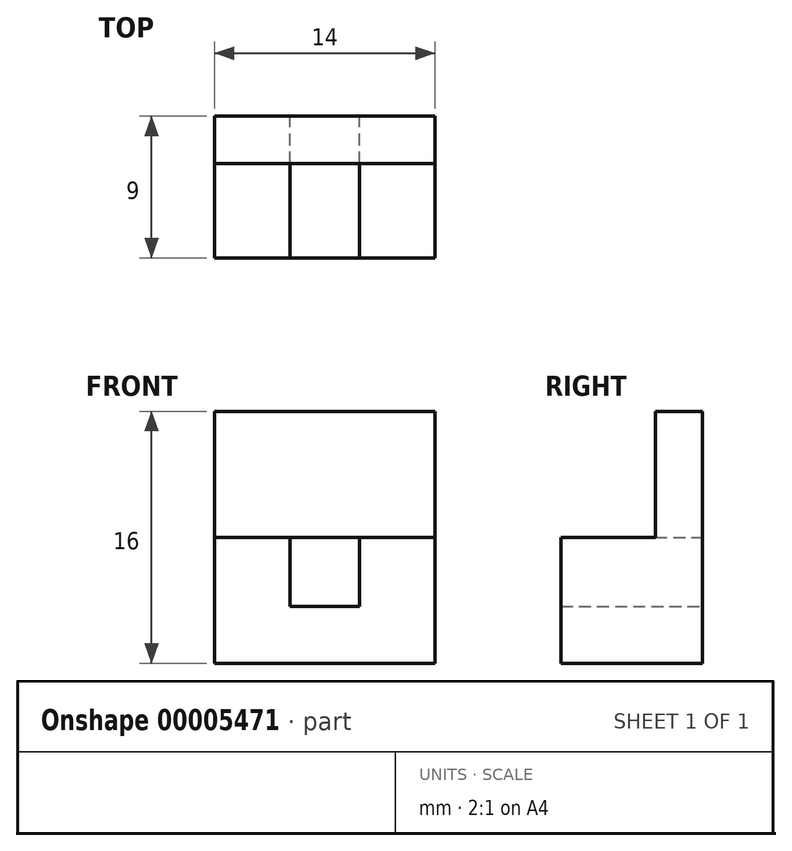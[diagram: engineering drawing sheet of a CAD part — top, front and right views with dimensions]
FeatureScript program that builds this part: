
annotation { "Feature Type Name" : "Feature", "Feature Type Description" : "" }
export const myFeature = defineFeature(function(context is Context, id is Id, definition is map)
    precondition{}
    {
        {
            var Q0;
            Q0=qCreatedBy(makeId("Front.planeOp"),FACE);
            var sketch = newSketch(context, id + "F0", { "sketchPlane" : qUnion([Q0])});
            skCircle(sketch, "E0.cCircle", {"center": v(0, 0) * mm, "radius": 2.2 * mm, "construction": true});
            skLineSegment(sketch, "E0.0", {"start": v(-2.2, 2.2) * mm, "end": v(2.2, 2.2) * mm});
            skLineSegment(sketch, "E0.1", {"start": v(2.2, 2.2) * mm, "end": v(2.2, -2.2) * mm});
            skLineSegment(sketch, "E0.2", {"start": v(2.2, -2.2) * mm, "end": v(-2.2, -2.2) * mm});
            skLineSegment(sketch, "E0.3", {"start": v(-2.2, -2.2) * mm, "end": v(-2.2, 2.2) * mm});
            skPoint(sketch, "E0.0.midPoint", {"position": v(0, 2.2) * mm});
            skLineSegment(sketch, "E1", {"start": v(-2.2, 2.2) * mm, "end": v(-7, 2.2) * mm});
            skLineSegment(sketch, "E2", {"start": v(-7, 2.2) * mm, "end": v(-7, -5.8) * mm});
            skLineSegment(sketch, "E3", {"start": v(-7, -5.8) * mm, "end": v(7, -5.8) * mm});
            skLineSegment(sketch, "E4", {"start": v(7, -5.8) * mm, "end": v(7, 2.2) * mm});
            skLineSegment(sketch, "E5", {"start": v(7, 2.2) * mm, "end": v(2.2, 2.2) * mm});
            skLineSegment(sketch, "E6", {"start": v(-7, 2.2) * mm, "end": v(-7, 10.2) * mm});
            skLineSegment(sketch, "E7", {"start": v(-7, 10.2) * mm, "end": v(7, 10.2) * mm});
            skLineSegment(sketch, "E8", {"start": v(7, 10.2) * mm, "end": v(7, 2.2) * mm});
            skSolve(sketch);
        }
        {
            var Q0;
            Q0=makeQuery(id+"F0.imprint","IMPRINT",FACE,{"disambiguationData":[TD([[makeQuery(id+"F0.imprint","IMPRINT",EDGE,{"derivedFrom":sQuery(id+"F0.wireOp",EDGE,"E0.1")}),1.0]])]});
            extrude(context, id + "F1", {"entities" : qUnion([Q0]), "depth" : 9 * mm});
        }
        {
            var Q0;
            Q0=makeQuery(id+"F0.imprint","IMPRINT",FACE,{"disambiguationData":[TD([[makeQuery(id+"F0.imprint","IMPRINT",EDGE,{"derivedFrom":sQuery(id+"F0.wireOp",EDGE,"E0.0")}),1.0]])]});
            extrude(context, id + "F2", {"entities" : qUnion([Q0]), "operationType" : NewBodyOperationType.ADD, "depth" : 3 * mm});
        }
    });
